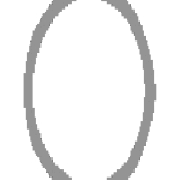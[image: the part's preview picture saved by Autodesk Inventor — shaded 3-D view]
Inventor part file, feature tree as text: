
AUTODESK INVENTOR PART (.ipt)
format: ipt  version: 2021 (Build 250183000, 183)  size: 110,080 bytes
history: native  units: in
note: dims shown in document units (in); Inventor stores cm internally (conversion verified against a paired STEP export)
features: other x4, sketch x3, plane x1
ambient origin geometry x8: Origin, YZ Plane, XZ Plane, XY Plane, X Axis, Y Axis, Z Axis, Center Point
bodies: Solid1 (feature_tree), Body (feature_tree)
feature tree (8):
  other  "Driven Length"
  other  "Frame Generator"
  other  "Start Plane"
  other  "End Plane"
  sketch  "Sketch"  dims[d2=15.5in d4=-0.0in d5=15.5in d6=0.12in d7=0.0in d8=90.0deg d9=15.5in]
  sketch  "Sketch2"  dims[d0=1.0in]
  plane  "Work Plane3"
  sketch  "Sketch3"  dims[d1=0.065in]
